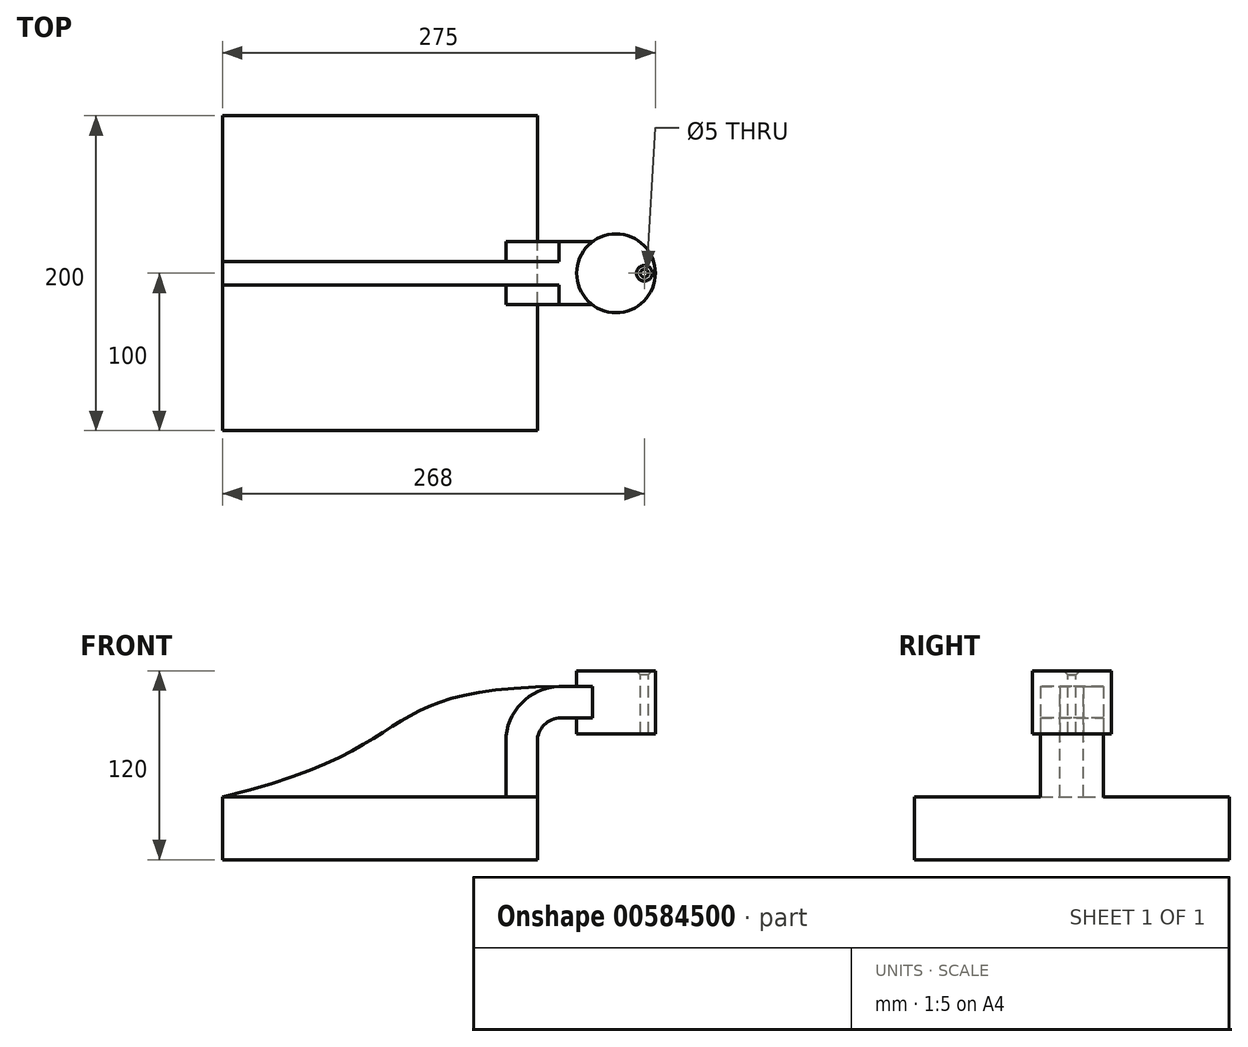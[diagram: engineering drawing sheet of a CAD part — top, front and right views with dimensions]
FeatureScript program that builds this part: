
annotation { "Feature Type Name" : "Feature", "Feature Type Description" : "" }
export const myFeature = defineFeature(function(context is Context, id is Id, definition is map)
    precondition{}
    {
        {
            var Q0;
            Q0=qCreatedBy(makeId("Front.planeOp"),FACE);
            var sketch = newSketch(context, id + "F0", { "sketchPlane" : qUnion([Q0])});
            skLineSegment(sketch, "E0.bottom", {"start": v(100, -20) * mm, "end": v(-100, -20) * mm});
            skLineSegment(sketch, "E0.top", {"start": v(100, 20) * mm, "end": v(-100, 20) * mm});
            skLineSegment(sketch, "E0.left", {"start": v(100, -20) * mm, "end": v(100, 20) * mm});
            skLineSegment(sketch, "E0.right", {"start": v(-100, -20) * mm, "end": v(-100, 20) * mm});
            skPoint(sketch, "E0.middle", {"position": v(0, 0) * mm});
            skLineSegment(sketch, "E1.bottom", {"start": v(175, 60) * mm, "end": v(125, 60) * mm});
            skLineSegment(sketch, "E1.top", {"start": v(175, 100) * mm, "end": v(125, 100) * mm});
            skLineSegment(sketch, "E1.left", {"start": v(175, 60) * mm, "end": v(175, 100) * mm});
            skLineSegment(sketch, "E1.right", {"start": v(125, 60) * mm, "end": v(125, 100) * mm});
            skPoint(sketch, "E1.middle", {"position": v(150, 80) * mm});
            skLineSegment(sketch, "E2", {"start": v(100, 20) * mm, "end": v(100, 55) * mm});
            skArc(sketch, "E3", {"start": v(100, 55) * mm, "mid": v(104.4, 65.6) * mm, "end": v(115, 70) * mm});
            skLineSegment(sketch, "E4", {"start": v(115, 70) * mm, "end": v(150, 70) * mm});
            skLineSegment(sketch, "E5.0", {"start": v(115, 90) * mm, "end": v(150, 90) * mm});
            skArc(sketch, "E5.1", {"start": v(80, 55) * mm, "mid": v(90.25, 79.75) * mm, "end": v(115, 90) * mm});
            skLineSegment(sketch, "E5.2", {"start": v(80, 20) * mm, "end": v(80, 55) * mm});
            skLineSegment(sketch, "E6", {"start": v(150, 60) * mm, "end": v(150, 100) * mm});
            skFitSpline(sketch, "E7", {"points": [v(-100, 20) * mm, v(125, 90) * mm], "startDerivative": vector(409.83, 96.91) * mm, "endDerivative": vector(409.84, -2.65) * mm});
            skSolve(sketch);
        }
        {
            var Q0;
            Q0=makeQuery(id+"F0.imprint","IMPRINT",FACE,{"disambiguationData":[TD([[makeQuery(id+"F0.imprint","IMPRINT",EDGE,{"derivedFrom":sQuery(id+"F0.wireOp",EDGE,"E0.bottom")}),-1.0]])]});
            extrude(context, id + "F1", {"entities" : qUnion([Q0]), "endBound" : BoundingType.SYMMETRIC, "depth" : 200 * mm, "offsetDistance" : 25 * mm});
        }
        {
            var Q0;
            {var subQ1=sQuery(id+"F0.wireOp",EDGE,"E2");Q0=makeQuery(id+"F0.imprint","IMPRINT",FACE,{"disambiguationData":[TD([[makeQuery(id+"F0.imprint","IMPRINT",EDGE,{"derivedFrom":subQ1}),1.0]])]});}
            var Q1;
            {var subQ3=sQuery(id+"F0.wireOp",EDGE,"E4");var subQ5=sQuery(id+"F0.wireOp",EDGE,"E6");var subQ6=makeQuery(id+"F0.imprint","INTERSECT",VERTEX,{"derivedFrom":[subQ3,subQ5]});Q1=makeQuery(id+"F0.imprint","IMPRINT",FACE,{"disambiguationData":[TD([[makeQuery(id+"F0.imprint","IMPRINT",EDGE,{"disambiguationData":[TD([[subQ6,1.0]])],"derivedFrom":subQ3}),1.0]])]});}
            extrude(context, id + "F2", {"entities" : qUnion([Q0, Q1]), "operationType" : NewBodyOperationType.ADD, "endBound" : BoundingType.SYMMETRIC, "depth" : 40 * mm, "offsetDistance" : 25 * mm});
        }
        {
            var Q0;
            {var subQ3=sQuery(id+"F0.wireOp",EDGE,"E5.2");Q0=makeQuery(id+"F0.imprint","IMPRINT",FACE,{"disambiguationData":[TD([[makeQuery(id+"F0.imprint","IMPRINT",EDGE,{"derivedFrom":subQ3}),1.0]])]});}
            extrude(context, id + "F3", {"entities" : qUnion([Q0]), "operationType" : NewBodyOperationType.ADD, "endBound" : BoundingType.SYMMETRIC, "depth" : 15 * mm, "offsetDistance" : 25 * mm});
        }
        {
            var Q0;
            {var subQ4=sQuery(id+"F0.wireOp",EDGE,"E1.left");Q0=makeQuery(id+"F0.imprint","IMPRINT",FACE,{"disambiguationData":[TD([[makeQuery(id+"F0.imprint","IMPRINT",EDGE,{"derivedFrom":subQ4}),1.0]])]});}
            var Q1;
            Q1=sQuery(id+"F0.wireOp",EDGE,"E6");
            revolve(context, id + "F4", {"operationType" : NewBodyOperationType.ADD, "entities" : qUnion([Q0]), "axis" : qUnion([Q1]), "revolveType" : RevolveType.FULL});
        }
        {
            var Q0;
            Q0=makeQuery(id+"F4.opRevolve","SWEPT_FACE",FACE,{"disambiguationData":[OSD([sQuery(id+"F0.wireOp",EDGE,"E1.top")])]});
            var sketch = newSketch(context, id + "F5", { "sketchPlane" : qUnion([Q0])});
            skLineSegment(sketch, "E8", {"start": v(150, 0) * mm, "end": v(168, 0) * mm});
            skSolve(sketch);
        }
        {
            var Q0;
            Q0=sQuery(id+"F5.wireOp",VERTEX,"E8.end");
            var Q1;
            Q1=makeQuery(id+"F1.opExtrude","SWEPT_BODY",BODY,{"disambiguationData":[OSD([sQuery(id+"F0.wireOp",EDGE,"E0.bottom"),sQuery(id+"F0.wireOp",EDGE,"E0.top"),sQuery(id+"F0.wireOp",EDGE,"E0.left"),sQuery(id+"F0.wireOp",EDGE,"E0.right")])]});
            hole(context, id + "F6", {"style" : HoleStyle.C_SINK, "endStyle" : HoleEndStyle.THROUGH, "holeDiameter" : 5 * mm, "cSinkDiameter" : 10 * mm, "cSinkAngle" : 90 * degree, "majorDiameter" : 5 * mm, "isTappedThrough" : true, "tappedDepth" : 12 * mm, "tapClearance" : 3, "startFromSketch" : true, "locations" : qUnion([Q0]), "scope" : qUnion([Q1])});
        }
    });
